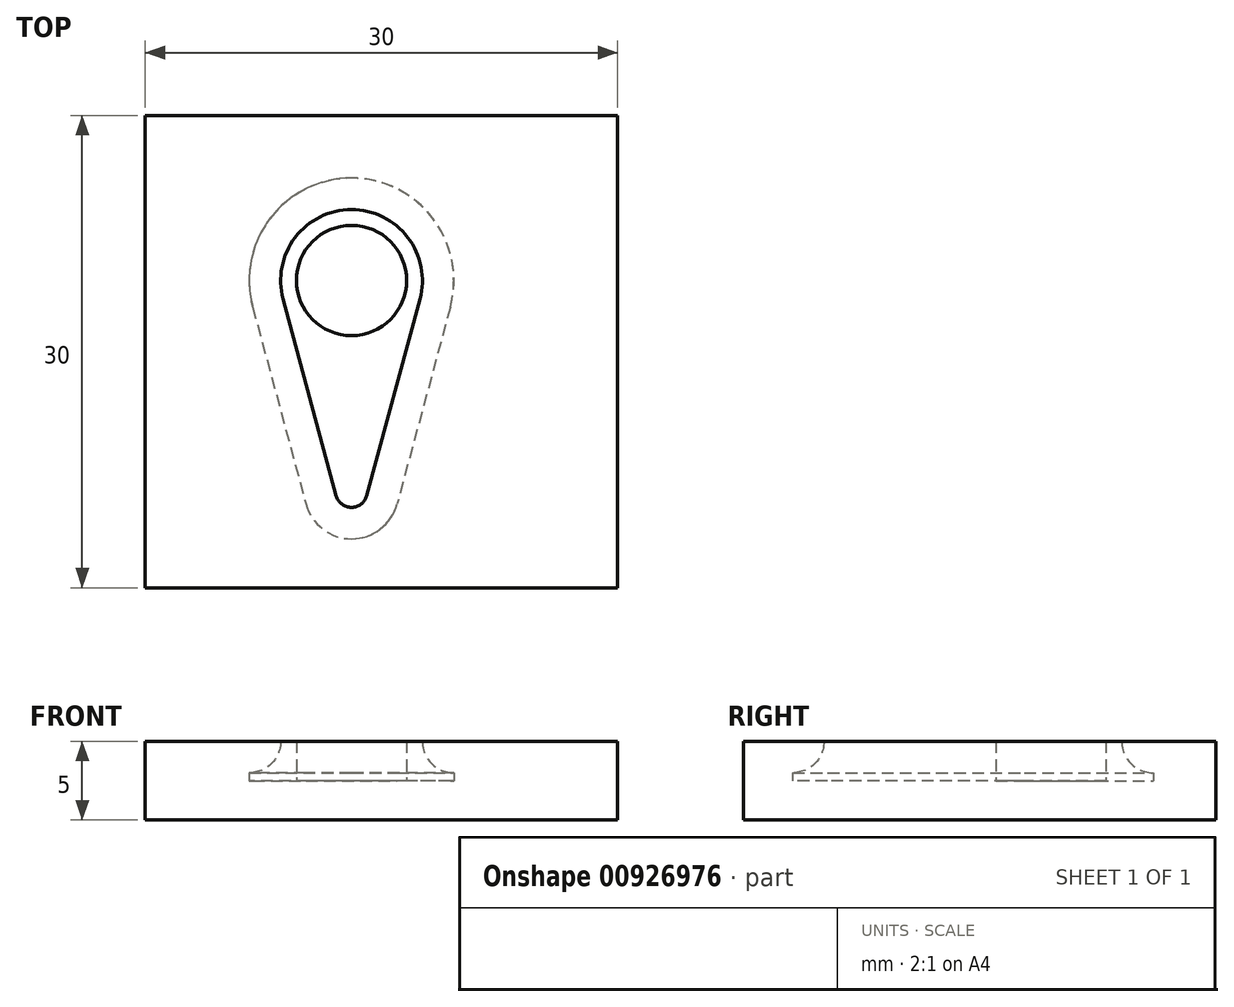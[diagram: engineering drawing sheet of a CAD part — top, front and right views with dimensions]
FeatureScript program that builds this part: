
annotation { "Feature Type Name" : "Feature", "Feature Type Description" : "" }
export const myFeature = defineFeature(function(context is Context, id is Id, definition is map)
    precondition{}
    {
        {
            var Q0;
            Q0=qCreatedBy(makeId("Top.planeOp"),FACE);
            var sketch = newSketch(context, id + "F0", { "sketchPlane" : qUnion([Q0])});
            skLineSegment(sketch, "E0", {"start": v(0, 71.12) * mm, "end": v(0, 6.5) * mm});
            skArc(sketch, "E1", {"start": v(0, 3.5) * mm, "mid": v(-3.5, 0) * mm, "end": v(0, -3.5) * mm});
            skArc(sketch, "E2", {"start": v(0, 6.5) * mm, "mid": v(-5.16, 3.95) * mm, "end": v(-6.27, -1.7) * mm});
            skLineSegment(sketch, "E3", {"start": v(0, 6.5) * mm, "end": v(0, -16.42) * mm});
            skArc(sketch, "E4", {"start": v(-2.9, -14.2) * mm, "mid": v(-1.82, -15.8) * mm, "end": v(0, -16.41) * mm});
            skLineSegment(sketch, "E5", {"start": v(-6.27, -1.7) * mm, "end": v(-2.9, -14.2) * mm});
            skSolve(sketch);
        }
        {
            var Q0;
            {var subQ1=sQuery(id+"F0.wireOp",EDGE,"E2");Q0=makeQuery(id+"F0.imprint","IMPRINT",FACE,{"disambiguationData":[TD([[makeQuery(id+"F0.imprint","IMPRINT",EDGE,{"derivedFrom":subQ1}),1.0]])]});}
            extrude(context, id + "F1", {"entities" : qUnion([Q0]), "depth" : 5 * mm, "offsetDistance" : 25 * mm});
        }
        {
            var Q0;
            Q0=makeQuery(id+"F1.opExtrude","SWEPT_EDGE",EDGE,{"disambiguationData":[OSD([sQuery(id+"F0.wireOp",EDGE,"E4"),sQuery(id+"F0.wireOp",EDGE,"E5")])]});
            cPlane(context, id + "F2", {"entities" : qUnion([Q0]), "cplaneType" : CPlaneType.LINE_ANGLE, "offset" : 25 * mm, "angle" : 75 * degree, "width" : 150 * mm, "height" : 150 * mm});
        }
        {
            var Q0;
            Q0=qCreatedBy(id+"F2.planeOp",FACE);
            var sketch = newSketch(context, id + "F3", { "sketchPlane" : qUnion([Q0])});
            skLineSegment(sketch, "E6.0", {"start": v(6.47, 4.5) * mm, "end": v(6.47, 0.5) * mm});
            skArc(sketch, "E7", {"start": v(6.47, 4.5) * mm, "mid": v(4.47, 2.5) * mm, "end": v(6.47, 0.5) * mm});
            skPoint(sketch, "E8.orphan", {"position": v(6.47, 5) * mm});
            skPoint(sketch, "E9.orphan", {"position": v(6.47, 0) * mm});
            skSolve(sketch);
        }
        {
            var Q0;
            Q0=qSketchRegion(id+"F3",true);
            var Q1;
            Q1=makeQuery(id+"F1.opExtrude","CAP_EDGE",EDGE,{"disambiguationData":[OSD([sQuery(id+"F0.wireOp",EDGE,"E4")])],"isStart":true});
            var Q2;
            Q2=makeQuery(id+"F1.opExtrude","CAP_EDGE",EDGE,{"disambiguationData":[OSD([sQuery(id+"F0.wireOp",EDGE,"E5")])],"isStart":true});
            var Q3;
            Q3=makeQuery(id+"F1.opExtrude","CAP_EDGE",EDGE,{"disambiguationData":[OSD([sQuery(id+"F0.wireOp",EDGE,"E2")])],"isStart":true});
            sweep(context, id + "F4", {"operationType" : NewBodyOperationType.REMOVE, "profiles" : qUnion([Q0]), "path" : qUnion([Q1, Q2, Q3])});
        }
        {
            var Q0;
            Q0=makeQuery(id+"F1.opExtrude","SWEPT_BODY",BODY,{"disambiguationData":[OSD([sQuery(id+"F0.wireOp",EDGE,"E1"),sQuery(id+"F0.wireOp",EDGE,"E2"),sQuery(id+"F0.wireOp",EDGE,"rY96AKfs-JU4n-LT8b-h3Ca-OXywf6S2JK09"),sQuery(id+"F0.wireOp",EDGE,"f2f6bcbf-8a26-4b1f-9b1e-a9f5522c723e.filletArc"),sQuery(id+"F0.wireOp",EDGE,"E3")])]});
            var Q1;
            Q1=qCreatedBy(makeId("Right.planeOp"),FACE);
            mirror(context, id + "F5", {"operationType" : NewBodyOperationType.ADD, "entities" : qUnion([Q0]), "mirrorPlane" : qUnion([Q1])});
        }
        {
            var Q0;
            Q0=qCreatedBy(makeId("Top.planeOp"),FACE);
            var sketch = newSketch(context, id + "F6", { "sketchPlane" : qUnion([Q0])});
            skLineSegment(sketch, "E10.bottom", {"start": v(-13.1, 10.48) * mm, "end": v(16.9, 10.48) * mm});
            skLineSegment(sketch, "E10.top", {"start": v(-13.1, -19.52) * mm, "end": v(16.9, -19.52) * mm});
            skLineSegment(sketch, "E10.left", {"start": v(-13.1, 10.48) * mm, "end": v(-13.1, -19.52) * mm});
            skLineSegment(sketch, "E10.right", {"start": v(16.9, 10.48) * mm, "end": v(16.9, -19.52) * mm});
            skSolve(sketch);
        }
        {
            var Q0;
            Q0 = qSketchRegion(id + "F6", true);
            extrude(context, id + "F7", {"entities" : qUnion([Q0]), "endBound" : BoundingType.SYMMETRIC, "depth" : 5 * mm, "offsetDistance" : 25 * mm});
        }
        {
            var Q0;
            Q0=makeQuery(id+"F1.opExtrude","SWEPT_BODY",BODY,{"disambiguationData":[OSD([sQuery(id+"F0.wireOp",EDGE,"E1"),sQuery(id+"F0.wireOp",EDGE,"E2"),sQuery(id+"F0.wireOp",EDGE,"E3"),sQuery(id+"F0.wireOp",EDGE,"E4"),sQuery(id+"F0.wireOp",EDGE,"E5")])]});
            var Q1;
            Q1=makeQuery(id+"F7.opExtrude","SWEPT_BODY",BODY,{"disambiguationData":[OSD([sQuery(id+"F6.wireOp",EDGE,"E10.bottom"),sQuery(id+"F6.wireOp",EDGE,"E10.top"),sQuery(id+"F6.wireOp",EDGE,"E10.left"),sQuery(id+"F6.wireOp",EDGE,"E10.right")])]});
            booleanBodies(context, id + "F8", {"operationType" : BooleanOperationType.SUBTRACTION, "tools" : qUnion([Q0]), "targets" : qUnion([Q1])});
        }
    });
